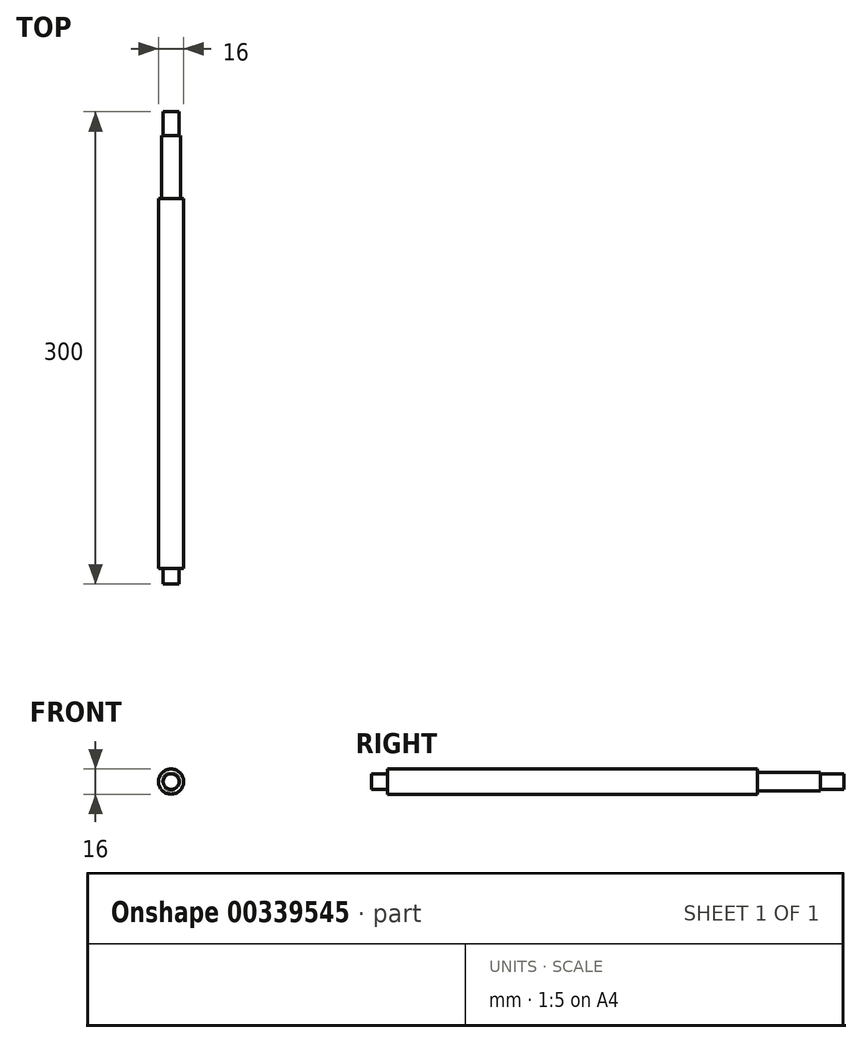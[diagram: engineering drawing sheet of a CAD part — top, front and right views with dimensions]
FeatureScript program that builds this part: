
annotation { "Feature Type Name" : "Feature", "Feature Type Description" : "" }
export const myFeature = defineFeature(function(context is Context, id is Id, definition is map)
    precondition{}
    {
        {
            var Q0;
            Q0=qCreatedBy(makeId("Front.planeOp"),FACE);
            var sketch = newSketch(context, id + "F0", { "sketchPlane" : qUnion([Q0])});
            skCircle(sketch, "E0", {"center": v(-6.17, 11.25) * mm, "radius": 6 * mm});
            skCircle(sketch, "E1", {"center": v(-6.17, 11.25) * mm, "radius": 8 * mm});
            skCircle(sketch, "E2", {"center": v(-6.17, 11.25) * mm, "radius": 5 * mm});
            skSolve(sketch);
        }
        {
            var Q0;
            Q0=makeQuery(id+"F0.imprint","IMPRINT",FACE,{"disambiguationData":[TD([[makeQuery(id+"F0.imprint","IMPRINT",EDGE,{"derivedFrom":sQuery(id+"F0.wireOp",EDGE,"E2")}),1.0]])]});
            var Q1;
            Q1=makeQuery(id+"F0.imprint","IMPRINT",FACE,{"disambiguationData":[TD([[makeQuery(id+"F0.imprint","IMPRINT",EDGE,{"derivedFrom":sQuery(id+"F0.wireOp",EDGE,"E0")}),-1.0]])]});
            var Q2;
            Q2=makeQuery(id+"F0.imprint","IMPRINT",FACE,{"disambiguationData":[TD([[makeQuery(id+"F0.imprint","IMPRINT",EDGE,{"derivedFrom":sQuery(id+"F0.wireOp",EDGE,"E0")}),1.0]])]});
            extrude(context, id + "F1", {"entities" : qUnion([Q0, Q1, Q2]), "flatOperationType" : FlatOperationType.REMOVE, "offsetDistance" : 25 * mm, "depth" : 235 * mm, "domain" : OperationDomain.MODEL});
        }
        {
            var Q0;
            Q0=makeQuery(id+"F0.imprint","IMPRINT",FACE,{"disambiguationData":[TD([[makeQuery(id+"F0.imprint","IMPRINT",EDGE,{"derivedFrom":sQuery(id+"F0.wireOp",EDGE,"E0")}),1.0]])]});
            var Q1;
            Q1=makeQuery(id+"F0.imprint","IMPRINT",FACE,{"disambiguationData":[TD([[makeQuery(id+"F0.imprint","IMPRINT",EDGE,{"derivedFrom":sQuery(id+"F0.wireOp",EDGE,"E2")}),1.0]])]});
            extrude(context, id + "F2", {"entities" : qUnion([Q0, Q1]), "operationType" : NewBodyOperationType.ADD, "flatOperationType" : FlatOperationType.REMOVE, "oppositeDirection" : true, "offsetDistance" : 25 * mm, "depth" : 40 * mm, "domain" : OperationDomain.MODEL});
        }
        {
            var Q0;
            Q0=makeQuery(id+"F2.opExtrude","CAP_FACE",FACE,{"disambiguationData":[OSD([sQuery(id+"F0.wireOp",EDGE,"E0")])],"isStart":false});
            var sketch = newSketch(context, id + "F3", { "sketchPlane" : qUnion([Q0])});
            skCircle(sketch, "E3", {"center": v(6.17, 11.25) * mm, "radius": 5 * mm});
            skSolve(sketch);
        }
        {
            var Q0;
            Q0=makeQuery(id+"F3.imprint","IMPRINT",FACE,{"disambiguationData":[TD([[makeQuery(id+"F3.imprint","IMPRINT",EDGE,{"derivedFrom":sQuery(id+"F3.wireOp",EDGE,"E3")}),1.0]])]});
            extrude(context, id + "F4", {"entities" : qUnion([Q0]), "operationType" : NewBodyOperationType.ADD, "flatOperationType" : FlatOperationType.REMOVE, "offsetDistance" : 25 * mm, "depth" : 15 * mm, "domain" : OperationDomain.MODEL});
        }
        {
            var Q0;
            Q0=makeQuery(id+"F1.opExtrude","CAP_FACE",FACE,{"disambiguationData":[OSD([sQuery(id+"F0.wireOp",EDGE,"E1")])],"isStart":false});
            var sketch = newSketch(context, id + "F5", { "sketchPlane" : qUnion([Q0])});
            skCircle(sketch, "E4", {"center": v(-6.17, 11.25) * mm, "radius": 5 * mm});
            skSolve(sketch);
        }
        {
            var Q0;
            Q0=makeQuery(id+"F5.imprint","IMPRINT",FACE,{"disambiguationData":[TD([[makeQuery(id+"F5.imprint","IMPRINT",EDGE,{"derivedFrom":sQuery(id+"F5.wireOp",EDGE,"E4")}),1.0]])]});
            extrude(context, id + "F6", {"entities" : qUnion([Q0]), "operationType" : NewBodyOperationType.ADD, "depth" : 10 * mm});
        }
    });
